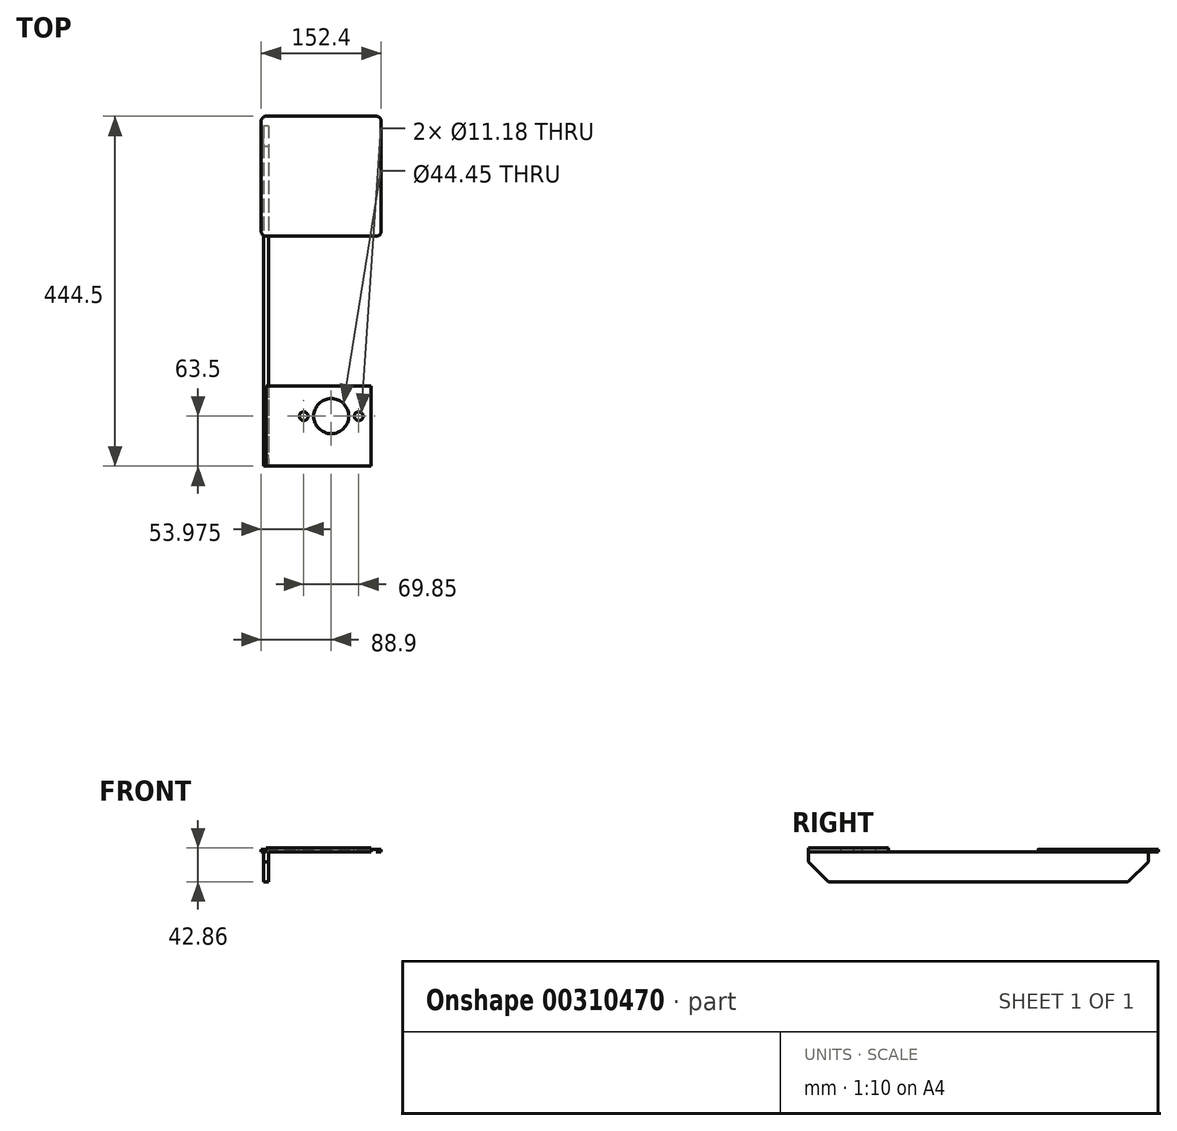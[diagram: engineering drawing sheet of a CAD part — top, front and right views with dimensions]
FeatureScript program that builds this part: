
annotation { "Feature Type Name" : "Feature", "Feature Type Description" : "" }
export const myFeature = defineFeature(function(context is Context, id is Id, definition is map)
    precondition{}
    {
        {
            var Q0;
            Q0=qCreatedBy(makeId("Top.planeOp"),FACE);
            var sketch = newSketch(context, id + "F0", { "sketchPlane" : qUnion([Q0])});
            skLineSegment(sketch, "E0.bottom", {"start": v(-3.17, 215.9) * mm, "end": v(3.18, 215.9) * mm});
            skLineSegment(sketch, "E0.top", {"start": v(-3.18, -215.9) * mm, "end": v(3.17, -215.9) * mm});
            skLineSegment(sketch, "E0.left", {"start": v(-3.17, 215.9) * mm, "end": v(-3.18, -215.9) * mm});
            skLineSegment(sketch, "E0.right", {"start": v(3.18, 215.9) * mm, "end": v(3.17, -215.9) * mm});
            skPoint(sketch, "E0.middle", {"position": v(0, 0) * mm});
            skSolve(sketch);
        }
        {
            var Q0;
            Q0 = qSketchRegion(id + "F0", true);
            extrude(context, id + "F1", {"entities" : qUnion([Q0]), "oppositeDirection" : true, "depth" : 38.1 * mm});
        }
        {
            var Q0;
            Q0=makeQuery(id+"F1.opExtrude","CAP_EDGE",EDGE,{"disambiguationData":[OSD([sQuery(id+"F0.wireOp",EDGE,"E0.top")])],"isStart":false});
            var Q1;
            Q1=makeQuery(id+"F1.opExtrude","CAP_EDGE",EDGE,{"disambiguationData":[OSD([sQuery(id+"F0.wireOp",EDGE,"E0.bottom")])],"isStart":false});
            chamfer(context, id + "F2", {"entities" : qUnion([Q0, Q1]), "width" : 25.4 * mm, "tangentPropagation" : true});
        }
        {
            var Q0;
            Q0=qCreatedBy(makeId("Top.planeOp"),FACE);
            var sketch = newSketch(context, id + "F3", { "sketchPlane" : qUnion([Q0])});
            skLineSegment(sketch, "E1.0.0", {"start": v(-3.17, 215.9) * mm, "end": v(-3.18, -215.9) * mm, "construction": true});
            skLineSegment(sketch, "E1.0.1", {"start": v(-3.18, -215.9) * mm, "end": v(3.17, -215.9) * mm, "construction": true});
            skLineSegment(sketch, "E1.0.2", {"start": v(3.17, -215.9) * mm, "end": v(3.18, 215.9) * mm, "construction": true});
            skLineSegment(sketch, "E1.0.3", {"start": v(3.18, 215.9) * mm, "end": v(-3.17, 215.9) * mm, "construction": true});
            skLineSegment(sketch, "E2.bottom", {"start": v(0, -215.9) * mm, "end": v(133.35, -215.9) * mm});
            skLineSegment(sketch, "E2.top", {"start": v(0, -114.3) * mm, "end": v(133.35, -114.3) * mm});
            skLineSegment(sketch, "E2.left", {"start": v(0, -215.9) * mm, "end": v(0, -114.3) * mm});
            skLineSegment(sketch, "E2.right", {"start": v(133.35, -215.9) * mm, "end": v(133.35, -114.3) * mm});
            skSolve(sketch);
        }
        {
            var Q0;
            Q0 = qSketchRegion(id + "F3", true);
            extrude(context, id + "F4", {"entities" : qUnion([Q0]), "operationType" : NewBodyOperationType.ADD, "depth" : 4.76 * mm});
        }
        {
            var Q0;
            Q0=makeQuery(id+"F4.opExtrude","CAP_FACE",FACE,{"disambiguationData":[OSD([sQuery(id+"F3.wireOp",EDGE,"E2.bottom"),sQuery(id+"F3.wireOp",EDGE,"E2.top"),sQuery(id+"F3.wireOp",EDGE,"E2.left"),sQuery(id+"F3.wireOp",EDGE,"E2.right")])],"isStart":false});
            var sketch = newSketch(context, id + "F5", { "sketchPlane" : qUnion([Q0])});
            skLineSegment(sketch, "E3", {"start": v(133.35, -165.1) * mm, "end": v(0, -165.1) * mm, "construction": true});
            skLineSegment(sketch, "E4.0", {"start": v(82.55, -203.2) * mm, "end": v(82.55, -101.6) * mm, "construction": true});
            skLineSegment(sketch, "E5.0", {"start": v(47.62, -203.2) * mm, "end": v(47.62, -101.6) * mm, "construction": true});
            skLineSegment(sketch, "E6.MirrorCS", {"start": v(117.47, -203.2) * mm, "end": v(117.47, -101.6) * mm, "construction": true});
            skCircle(sketch, "E7", {"center": v(82.55, -152.4) * mm, "radius": 22.23 * mm});
            skCircle(sketch, "E8", {"center": v(47.62, -152.4) * mm, "radius": 5.59 * mm});
            skCircle(sketch, "E9", {"center": v(117.47, -152.4) * mm, "radius": 5.59 * mm});
            skSolve(sketch);
        }
        {
            var Q0;
            Q0 = qSketchRegion(id + "F5", true);
            extrude(context, id + "F6", {"entities" : qUnion([Q0]), "operationType" : NewBodyOperationType.REMOVE, "oppositeDirection" : true, "depth" : 25.4 * mm});
        }
        {
            var Q0;
            Q0=makeQuery(id+"F1.opExtrude","CAP_FACE",FACE,{"disambiguationData":[OSD([sQuery(id+"F0.wireOp",EDGE,"E0.bottom"),sQuery(id+"F0.wireOp",EDGE,"E0.top"),sQuery(id+"F0.wireOp",EDGE,"E0.left"),sQuery(id+"F0.wireOp",EDGE,"E0.right")])],"isStart":true});
            var sketch = newSketch(context, id + "F7", { "sketchPlane" : qUnion([Q0])});
            skLineSegment(sketch, "E10.0", {"start": v(-6.35, 228.6) * mm, "end": v(-6.35, -203.2) * mm, "construction": true});
            skLineSegment(sketch, "E11.bottom", {"start": v(-6.35, 228.6) * mm, "end": v(146.05, 228.6) * mm});
            skLineSegment(sketch, "E11.top", {"start": v(-6.35, 76.2) * mm, "end": v(146.05, 76.2) * mm});
            skLineSegment(sketch, "E11.left", {"start": v(-6.35, 228.6) * mm, "end": v(-6.35, 76.2) * mm});
            skLineSegment(sketch, "E11.right", {"start": v(146.05, 228.6) * mm, "end": v(146.05, 76.2) * mm});
            skSolve(sketch);
        }
        {
            var Q0;
            Q0 = qSketchRegion(id + "F7", true);
            extrude(context, id + "F8", {"entities" : qUnion([Q0]), "operationType" : NewBodyOperationType.ADD, "depth" : 3.17 * mm});
        }
        {
            var Q0;
            Q0=makeQuery(id+"F8.opExtrude","SWEPT_EDGE",EDGE,{"disambiguationData":[OSD([sQuery(id+"F7.wireOp",EDGE,"E11.top"),sQuery(id+"F7.wireOp",EDGE,"E11.right")])]});
            var Q1;
            Q1=makeQuery(id+"F8.opExtrude","SWEPT_EDGE",EDGE,{"disambiguationData":[OSD([sQuery(id+"F7.wireOp",EDGE,"E11.top"),sQuery(id+"F7.wireOp",EDGE,"E11.left")])]});
            var Q2;
            Q2=makeQuery(id+"F8.opExtrude","SWEPT_EDGE",EDGE,{"disambiguationData":[OSD([sQuery(id+"F7.wireOp",EDGE,"E11.bottom"),sQuery(id+"F7.wireOp",EDGE,"E11.right")])]});
            var Q3;
            Q3=makeQuery(id+"F8.opExtrude","SWEPT_EDGE",EDGE,{"disambiguationData":[OSD([sQuery(id+"F7.wireOp",EDGE,"E11.bottom"),sQuery(id+"F7.wireOp",EDGE,"E11.left")])]});
            fillet(context, id + "F9", {"entities" : qUnion([Q0, Q1, Q2, Q3]), "radius" : 6.35 * mm, "tangentPropagation" : true, "allowEdgeOverflow" : false});
        }
    });
